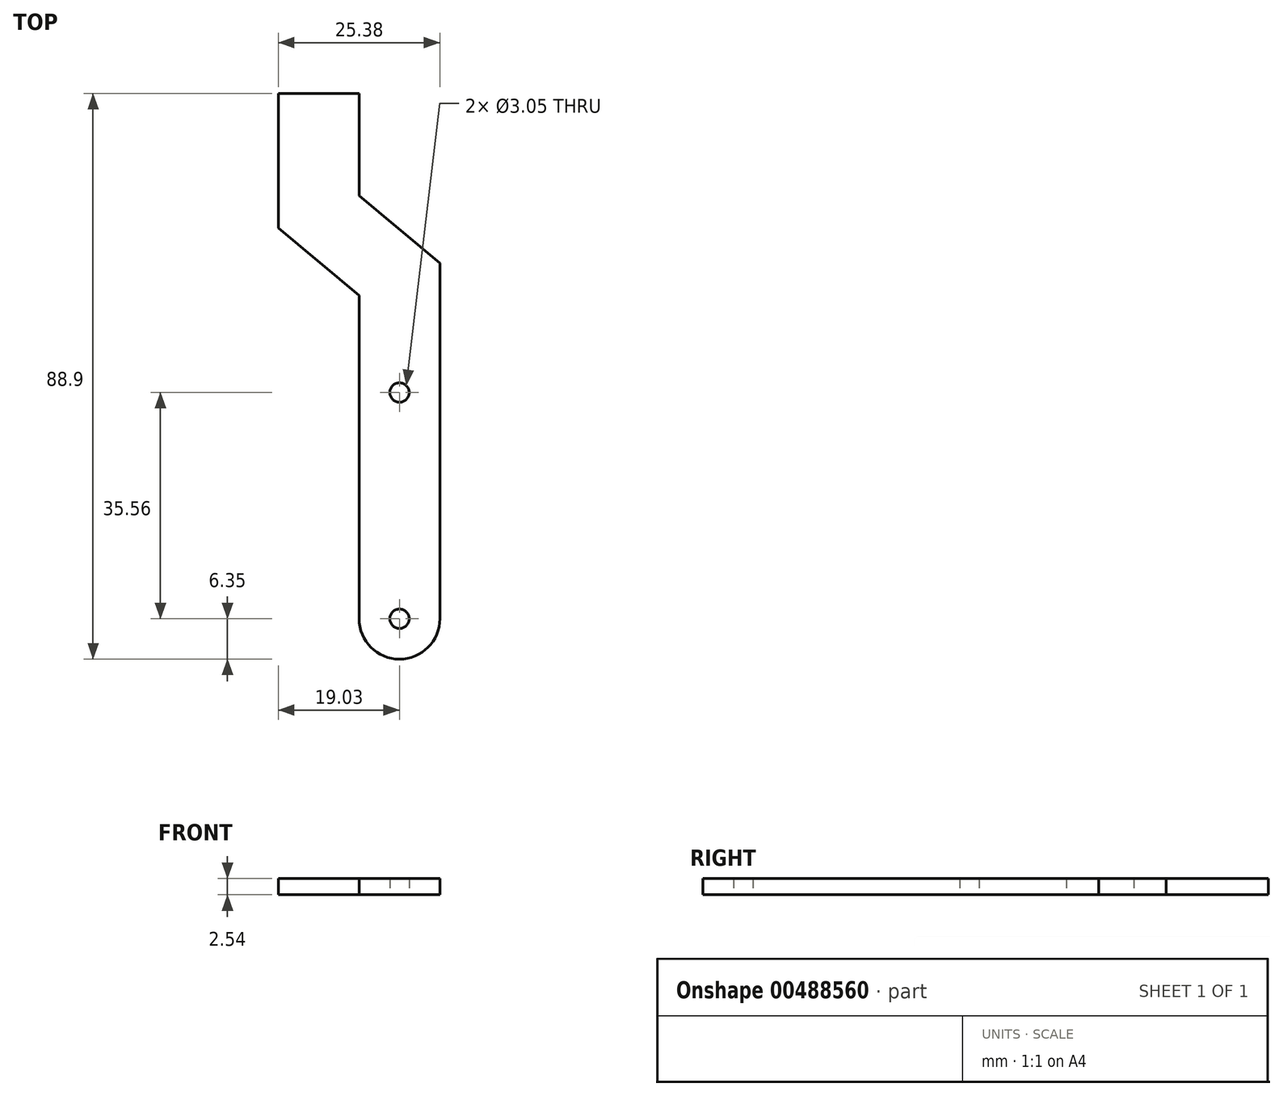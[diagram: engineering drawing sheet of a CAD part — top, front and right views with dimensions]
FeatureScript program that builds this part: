
annotation { "Feature Type Name" : "Feature", "Feature Type Description" : "" }
export const myFeature = defineFeature(function(context is Context, id is Id, definition is map)
    precondition{}
    {
        {
            var Q0;
            Q0=qCreatedBy(makeId("Top.planeOp"),FACE);
            var sketch = newSketch(context, id + "F0", { "sketchPlane" : qUnion([Q0])});
            skLineSegment(sketch, "E0.top", {"start": v(0, -25.4) * mm, "end": v(0, -25.4) * mm});
            skLineSegment(sketch, "E0.right", {"start": v(-6.35, 31.75) * mm, "end": v(-6.35, -19.05) * mm});
            skPoint(sketch, "E0.middle", {"position": v(0, 0) * mm});
            skPoint(sketch, "E1.visualSharp", {"position": v(-6.35, -25.4) * mm});
            skArc(sketch, "E1.filletArc", {"start": v(-6.35, -19.05) * mm, "mid": v(-4.5, -23.54) * mm, "end": v(0, -25.4) * mm});
            skPoint(sketch, "E2.visualSharp", {"position": v(6.35, -25.4) * mm});
            skArc(sketch, "E2.filletArc", {"start": v(0, -25.4) * mm, "mid": v(4.5, -23.54) * mm, "end": v(6.35, -19.05) * mm});
            skCircle(sketch, "E3", {"center": v(0, -19.05) * mm, "radius": 1.52 * mm});
            skCircle(sketch, "E4", {"center": v(0, 16.51) * mm, "radius": 1.52 * mm});
            skPoint(sketch, "E5.visualSharp", {"position": v(6.35, 25.4) * mm});
            skLineSegment(sketch, "E6", {"start": v(-6.35, 57.15) * mm, "end": v(-6.35, 63.5) * mm});
            skLineSegment(sketch, "E7", {"start": v(-6.35, 63.5) * mm, "end": v(-19.03, 63.5) * mm});
            skLineSegment(sketch, "E8", {"start": v(-19.03, 63.5) * mm, "end": v(-19.03, 42.34) * mm});
            skLineSegment(sketch, "E9", {"start": v(-19.03, 42.34) * mm, "end": v(-6.35, 31.75) * mm});
            skLineSegment(sketch, "E10", {"start": v(-6.35, 47.43) * mm, "end": v(6.35, 36.83) * mm});
            skLineSegment(sketch, "E11", {"start": v(-6.35, 47.43) * mm, "end": v(-6.35, 63.5) * mm});
            skLineSegment(sketch, "E12", {"start": v(6.35, 36.83) * mm, "end": v(6.35, -19.05) * mm});
            skSolve(sketch);
        }
        {
            var Q0;
            Q0=makeQuery(id+"F0.imprint","IMPRINT",FACE,{"disambiguationData":[TD([[makeQuery(id+"F0.imprint","IMPRINT",EDGE,{"derivedFrom":sQuery(id+"F0.wireOp",EDGE,"E0.left")}),-1.0]])]});
            var Q1;
            Q1=makeQuery(id+"F0.imprint","IMPRINT",FACE,{"disambiguationData":[TD([[makeQuery(id+"F0.imprint","IMPRINT",EDGE,{"derivedFrom":sQuery(id+"F0.wireOp",EDGE,"E0.right")}),1.0]])]});
            extrude(context, id + "F1", {"entities" : qUnion([Q0, Q1]), "depth" : 2.54 * mm});
        }
    });
